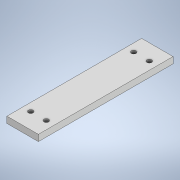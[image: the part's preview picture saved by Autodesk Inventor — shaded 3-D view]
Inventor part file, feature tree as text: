
AUTODESK INVENTOR PART (.ipt)
format: ipt  version: 2022 (Build 260153000, 153)  size: 110,080 bytes
history: native  units: mm
features: extrude x1, sketch x1
ambient origin geometry x8: Origin, YZ Plane, XZ Plane, XY Plane, X Axis, Y Axis, Z Axis, Center Point
bodies: Body1 (feature_tree)
feature tree (2):
  extrude  "Extrusão3"  Depth=4.0mm
  sketch  "Esboço1"  dims[d15=3.0mm d16=3.0mm d17=3.0mm d18=3.0mm d19=10.0mm d20=5.0mm d21=5.0mm d22=10.0mm d23=5.0mm d24=5.0mm d25=10.0mm d26=10.0mm d27=4.0mm d28=0.0mm]
